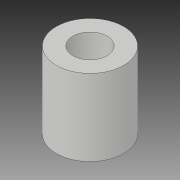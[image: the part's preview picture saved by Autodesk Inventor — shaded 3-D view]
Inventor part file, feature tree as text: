
AUTODESK INVENTOR PART (.ipt)
format: ipt  version: 2018 (Build 220112000, 112)  size: 94,720 bytes
history: native  units: in
note: dims shown in document units (in); Inventor stores cm internally (conversion verified against a paired STEP export)
features: extrude x1, sketch x1
ambient origin geometry x8: Origin, YZ Plane, XZ Plane, XY Plane, X Axis, Y Axis, Z Axis, Center Point
bodies: Solid1 (feature_tree)
feature tree (2):
  extrude  "Extrusion1"  Depth=0.85in TaperAngle=0.0deg
  sketch  "Sketch1"  dims[d0=0.75in d1=0.85in d2=0.0in d3=0.38in]
